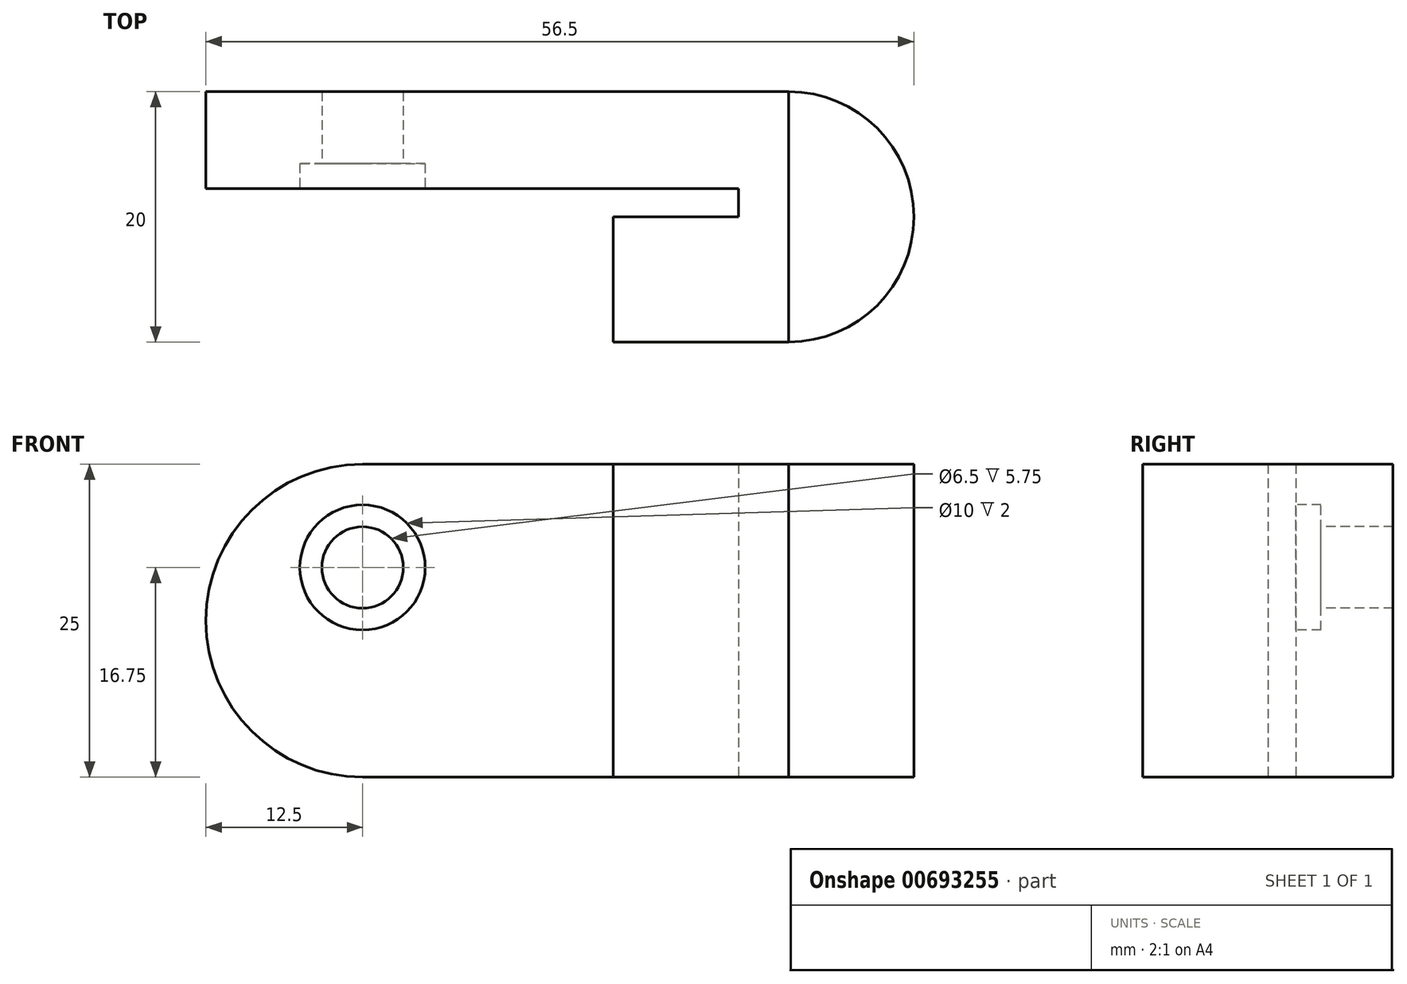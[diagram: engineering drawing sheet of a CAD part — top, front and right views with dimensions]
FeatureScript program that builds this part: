
annotation { "Feature Type Name" : "Feature", "Feature Type Description" : "" }
export const myFeature = defineFeature(function(context is Context, id is Id, definition is map)
    precondition{}
    {
        {
            var Q0;
            Q0=qCreatedBy(makeId("Top.planeOp"),FACE);
            var sketch = newSketch(context, id + "F0", { "sketchPlane" : qUnion([Q0])});
            skLineSegment(sketch, "E0.bottom", {"start": v(-7, -5) * mm, "end": v(7, -5) * mm});
            skLineSegment(sketch, "E0.top", {"start": v(-7, 5) * mm, "end": v(7, 5) * mm});
            skLineSegment(sketch, "E0.left", {"start": v(-7, -5) * mm, "end": v(-7, 5) * mm});
            skLineSegment(sketch, "E0.right", {"start": v(7, -5) * mm, "end": v(7, 5) * mm});
            skPoint(sketch, "E0.middle", {"position": v(0, 0) * mm});
            skSolve(sketch);
        }
        {
            var Q0;
            Q0=makeQuery(id+"F0.imprint","IMPRINT",FACE,{"disambiguationData":[TD([[makeQuery(id+"F0.imprint","IMPRINT",EDGE,{"derivedFrom":sQuery(id+"F0.wireOp",EDGE,"E0.bottom")}),1.0]])]});
            extrude(context, id + "F1", {"entities" : qUnion([Q0]), "depth" : 25 * mm, "offsetDistance" : 25 * mm});
        }
        {
            var Q0;
            Q0=makeQuery(id+"F1.opExtrude","SWEPT_FACE",FACE,{"disambiguationData":[OSD([sQuery(id+"F0.wireOp",EDGE,"E0.top")])]});
            var sketch = newSketch(context, id + "F2", { "sketchPlane" : qUnion([Q0])});
            skLineSegment(sketch, "E1.bottom", {"start": v(-7, 25) * mm, "end": v(-3, 25) * mm});
            skLineSegment(sketch, "E1.top", {"start": v(-7, 0) * mm, "end": v(-3, 0) * mm});
            skLineSegment(sketch, "E1.left", {"start": v(-7, 25) * mm, "end": v(-7, 0) * mm});
            skLineSegment(sketch, "E1.right", {"start": v(-3, 25) * mm, "end": v(-3, 0) * mm});
            skSolve(sketch);
        }
        {
            var Q0;
            Q0=makeQuery(id+"F2.imprint","IMPRINT",FACE,{"disambiguationData":[TD([[makeQuery(id+"F2.imprint","IMPRINT",EDGE,{"derivedFrom":sQuery(id+"F2.wireOp",EDGE,"E1.bottom")}),1.0]])]});
            extrude(context, id + "F3", {"entities" : qUnion([Q0]), "operationType" : NewBodyOperationType.ADD, "depth" : 10 * mm, "offsetDistance" : 25 * mm});
        }
        {
            var Q0;
            Q0=makeQuery(id+"F3.opExtrude","SWEPT_FACE",FACE,{"disambiguationData":[OSD([sQuery(id+"F2.wireOp",EDGE,"E1.right")])]});
            var sketch = newSketch(context, id + "F4", { "sketchPlane" : qUnion([Q0])});
            skLineSegment(sketch, "E2.bottom", {"start": v(-15, 25) * mm, "end": v(-7.25, 25) * mm});
            skLineSegment(sketch, "E2.top", {"start": v(-15, 0) * mm, "end": v(-7.25, 0) * mm});
            skLineSegment(sketch, "E2.left", {"start": v(-15, 25) * mm, "end": v(-15, 0) * mm});
            skLineSegment(sketch, "E2.right", {"start": v(-7.25, 25) * mm, "end": v(-7.25, 0) * mm});
            skSolve(sketch);
        }
        {
            var Q0;
            Q0=makeQuery(id+"F4.imprint","IMPRINT",FACE,{"disambiguationData":[TD([[makeQuery(id+"F4.imprint","IMPRINT",EDGE,{"derivedFrom":sQuery(id+"F4.wireOp",EDGE,"E2.bottom")}),-1.0]])]});
            extrude(context, id + "F5", {"entities" : qUnion([Q0]), "operationType" : NewBodyOperationType.ADD, "depth" : 30 * mm, "offsetDistance" : 25 * mm});
        }
        {
            var Q0;
            Q0=makeQuery(id+"F5.boolean.opBoolean","MERGE",FACE,{"derivedFrom":[makeQuery(id+"F3.boolean.opBoolean","MERGE",FACE,{"derivedFrom":[makeQuery(id+"F1.opExtrude","CAP_FACE",FACE,{"disambiguationData":[OSD([sQuery(id+"F0.wireOp",EDGE,"E0.bottom"),sQuery(id+"F0.wireOp",EDGE,"E0.top"),sQuery(id+"F0.wireOp",EDGE,"E0.left"),sQuery(id+"F0.wireOp",EDGE,"E0.right")])],"isStart":false}),makeQuery(id+"F3.opExtrude","SWEPT_FACE",FACE,{"disambiguationData":[OSD([sQuery(id+"F2.wireOp",EDGE,"E1.bottom")])]})]}),makeQuery(id+"F5.opExtrude","SWEPT_FACE",FACE,{"disambiguationData":[OSD([sQuery(id+"F4.wireOp",EDGE,"E2.bottom")])]})]});
            var sketch = newSketch(context, id + "F6", { "sketchPlane" : qUnion([Q0])});
            skArc(sketch, "E3", {"start": v(7, -5) * mm, "mid": v(17, 5) * mm, "end": v(7, 15) * mm});
            skSolve(sketch);
        }
        {
            var Q0;
            Q0=makeQuery(id+"F6.imprint","IMPRINT",FACE,{"disambiguationData":[TD([[makeQuery(id+"F6.imprint","IMPRINT",EDGE,{"derivedFrom":sQuery(id+"F6.wireOp",EDGE,"E3")}),1.0]])]});
            extrude(context, id + "F7", {"entities" : qUnion([Q0]), "oppositeDirection" : true, "depth" : 25 * mm, "offsetDistance" : 25 * mm});
        }
        {
            var Q0;
            Q0=makeQuery(id+"F5.opExtrude","SWEPT_FACE",FACE,{"disambiguationData":[OSD([sQuery(id+"F4.wireOp",EDGE,"E2.right")])]});
            var sketch = newSketch(context, id + "F8", { "sketchPlane" : qUnion([Q0])});
            skArc(sketch, "E4", {"start": v(-27, 25) * mm, "mid": v(-39.5, 12.5) * mm, "end": v(-27, 0) * mm});
            skSolve(sketch);
        }
        {
            var Q0;
            Q0=makeQuery(id+"F8.imprint","IMPRINT",FACE,{"disambiguationData":[TD([[makeQuery(id+"F8.imprint","IMPRINT",EDGE,{"derivedFrom":sQuery(id+"F8.wireOp",EDGE,"E4")}),1.0]])]});
            extrude(context, id + "F9", {"entities" : qUnion([Q0]), "operationType" : NewBodyOperationType.ADD, "oppositeDirection" : true, "depth" : 7.75 * mm, "offsetDistance" : 25 * mm});
        }
        {
            var Q0;
            {var subQ0=sQuery(id+"F4.wireOp",EDGE,"E2.right");Q0=makeQuery(id+"F9.boolean.opBoolean","MERGE",FACE,{"derivedFrom":[makeQuery(id+"F5.opExtrude","SWEPT_FACE",FACE,{"disambiguationData":[OSD([subQ0])]}),makeQuery(id+"F9.opExtrude","CAP_FACE",FACE,{"disambiguationData":[OSD([subQ0,sQuery(id+"F8.wireOp",EDGE,"E4")])],"isStart":true})]});}
            var sketch = newSketch(context, id + "F10", { "sketchPlane" : qUnion([Q0])});
            skCircle(sketch, "E5", {"center": v(-27, 16.75) * mm, "radius": 3.25 * mm});
            skCircle(sketch, "E6", {"center": v(-27, 16.75) * mm, "radius": 5 * mm});
            skSolve(sketch);
        }
        {
            var Q0;
            Q0=makeQuery(id+"F10.imprint","IMPRINT",FACE,{"disambiguationData":[TD([[makeQuery(id+"F10.imprint","IMPRINT",EDGE,{"derivedFrom":sQuery(id+"F10.wireOp",EDGE,"E5")}),1.0]])]});
            extrude(context, id + "F11", {"entities" : qUnion([Q0]), "operationType" : NewBodyOperationType.REMOVE, "endBound" : BoundingType.THROUGH_ALL, "oppositeDirection" : true, "depth" : 25 * mm, "offsetDistance" : 25 * mm});
        }
        {
            var Q0;
            Q0=makeQuery(id+"F10.imprint","IMPRINT",FACE,{"disambiguationData":[TD([[makeQuery(id+"F10.imprint","IMPRINT",EDGE,{"derivedFrom":sQuery(id+"F10.wireOp",EDGE,"E5")}),-1.0]])]});
            extrude(context, id + "F12", {"entities" : qUnion([Q0]), "operationType" : NewBodyOperationType.REMOVE, "oppositeDirection" : true, "depth" : 2 * mm, "offsetDistance" : 25 * mm});
        }
    });
